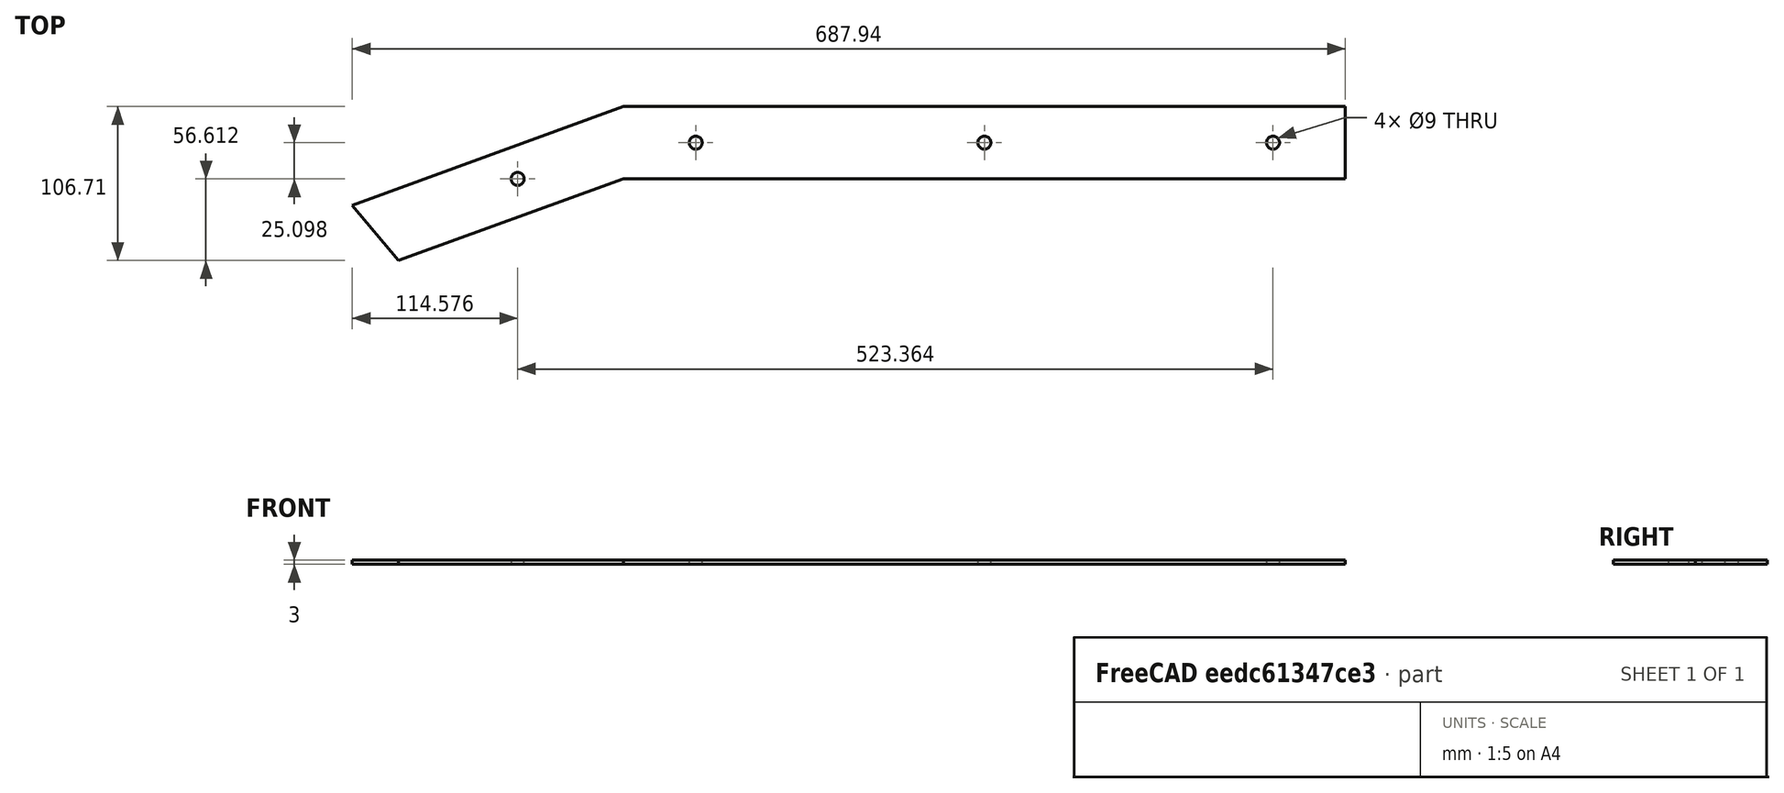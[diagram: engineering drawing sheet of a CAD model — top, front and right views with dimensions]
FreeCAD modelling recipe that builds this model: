
FCSTD DOCUMENT  (FreeCAD 0.20R29177 +426 (Git))
Label: faux
License: All rights reserved
LicenseURL: http://en.wikipedia.org/wiki/All_rights_reserved
objects: Sketcher::SketchObject×2, PartDesign::Pad×1, PartDesign::Body×1
note: 5 computed .brp shape members not serialized (recipe doc carries the construction recipe); baked Part::Feature solids carry a one-line shape summary decoded from their .brp

FEATURE [Sketcher::SketchObject] Sketch
  FullyConstrained = true
  MapMode = 5
  Support = -> [XY_Plane]
  sketch-geometry (10):
    g0: LineSegment StartX=0 StartY=50 StartZ=0 EndX=-500 EndY=50 EndZ=0
    g1: LineSegment StartX=-500 StartY=0 StartZ=0 EndX=0 EndY=0 EndZ=0
    g2: LineSegment StartX=-500 StartY=50 StartZ=0 EndX=-687.939 EndY=-18.404 EndZ=0
    g3: LineSegment StartX=-500 StartY=0 StartZ=0 EndX=-655.799 EndY=-56.7063 EndZ=0
    g4: LineSegment StartX=0 StartY=50 StartZ=0 EndX=0 EndY=0 EndZ=0
    g5: LineSegment StartX=-687.939 StartY=-18.404 StartZ=0 EndX=-655.799 EndY=-56.7063 EndZ=0
    g6: Circle CenterX=-50 CenterY=25 CenterZ=0 NormalX=0 NormalY=0 NormalZ=1 AngleXU=0 Radius=4.5
    g7: Circle CenterX=-250 CenterY=25 CenterZ=0 NormalX=0 NormalY=0 NormalZ=1 AngleXU=0 Radius=4.5
    g8: Circle CenterX=-450 CenterY=25 CenterZ=0 NormalX=0 NormalY=0 NormalZ=1 AngleXU=0 Radius=4.5
    g9: Circle CenterX=-573.364 CenterY=-0.0980378 CenterZ=0 NormalX=0 NormalY=0 NormalZ=1 AngleXU=0 Radius=4.5
  constraints (29):
    c: Coincident(g3,g1)
    c: Coincident(g2,g0)
    c: Angle(g2,g0) = 2.79253
    c: Angle(g3,g1) = 2.79253
    c: Coincident(g0,g4)
    c: Coincident(g1,g4)
    c: Distance(g5,g5) = 50
    c: Distance(g1,g0) = 50
    c: Coincident(g5,g3)
    c: Coincident(g5,g2)
    c: Distance(g0) = 500
    c: Distance(g2) = 200
    c: Distance(g0,g1) = 50
    c: Coincident(g1,g-1)
    c: PointOnObject(g1,g-1)
    c: Parallel(g0,g1)
    c: PointOnObject(g0,g-2)
    c: DistanceX(g6,g1) = 50
    c: DistanceX(g1,g8) = 50
    c: DistanceX(g7,g1) = 250
    c: Distance(g9,g3) = 100
    c: Distance(g9,g3) = 25
    c: DistanceY(g8,g0) = 25
    c: DistanceY(g7,g0) = 25
    c: DistanceY(g6,g0) = 25
    c: Equal(g9,g8)
    c: Equal(g9,g7)
    c: Equal(g9,g6)
    c: Diameter(g9) = 9
FEATURE [PartDesign::Pad] Pad
  Direction = (0,0,1)
  Length = 3
  Length2 = 10
  Profile = -> Sketch
  ReferenceAxis = -> Sketch [N_Axis]
  Type = 0
FEATURE [Sketcher::SketchObject] Sketch001
  FullyConstrained = false
  MapMode = 5
  Placement = pos=(0,0,0) rot=(0.57735,0.57735,0.57735;2.0944rad)
  Support = -> [Pad]
  sketch-geometry (9):
    g0: LineSegment StartX=50 StartY=100 StartZ=0 EndX=-50 EndY=100 EndZ=0
    g1: LineSegment StartX=-50 StartY=100 StartZ=0 EndX=-50 EndY=0 EndZ=0
    g2: LineSegment StartX=-50 StartY=0 StartZ=0 EndX=50 EndY=0 EndZ=0
    g3: LineSegment StartX=50 StartY=0 StartZ=0 EndX=50 EndY=100 EndZ=0
    g4: Circle CenterX=50 CenterY=0 CenterZ=0 NormalX=0 NormalY=0 NormalZ=1 AngleXU=0 Radius=100
    g5: LineSegment StartX=-50 StartY=100 StartZ=0 EndX=50 EndY=0 EndZ=0
    g6: Circle CenterX=-20.7107 CenterY=70.7107 CenterZ=0 NormalX=0 NormalY=0 NormalZ=1 AngleXU=0 Radius=32.8781
    g7: LineSegment StartX=-7.73503 StartY=100 StartZ=0 EndX=50 EndY=0 EndZ=0
    g8: LineSegment StartX=-200.52 StartY=127.63 StartZ=0 EndX=218.436 EndY=-83.2797 EndZ=0
  constraints (20):
    c: Coincident(g0,g1)
    c: Coincident(g1,g2)
    c: Coincident(g2,g3)
    c: Coincident(g3,g0)
    c: Horizontal(g0)
    c: Vertical(g1)
    c: Vertical(g3)
    c: Distance(g2) = 100
    c: Distance(g3) = 100
    c: Symmetric(g1,g2,g-2)
    c: PointOnObject(g1,g-1)
    c: Coincident(g4,g2)
    c: Radius(g4) = 100
    c: Coincident(g5,g2)
    c: Coincident(g5,g0)
    c: PointOnObject(g6,g5)
    c: PointOnObject(g6,g4)
    c: Coincident(g7,g2)
    c: Angle(g3,g7) = 0.523599
    c: PointOnObject(g7,g0)
FEATURE [PartDesign::Body] Body
  Group = -> [Sketch,Pad,Sketch001]
  Origin = -> Origin
  Tip = -> Pad
